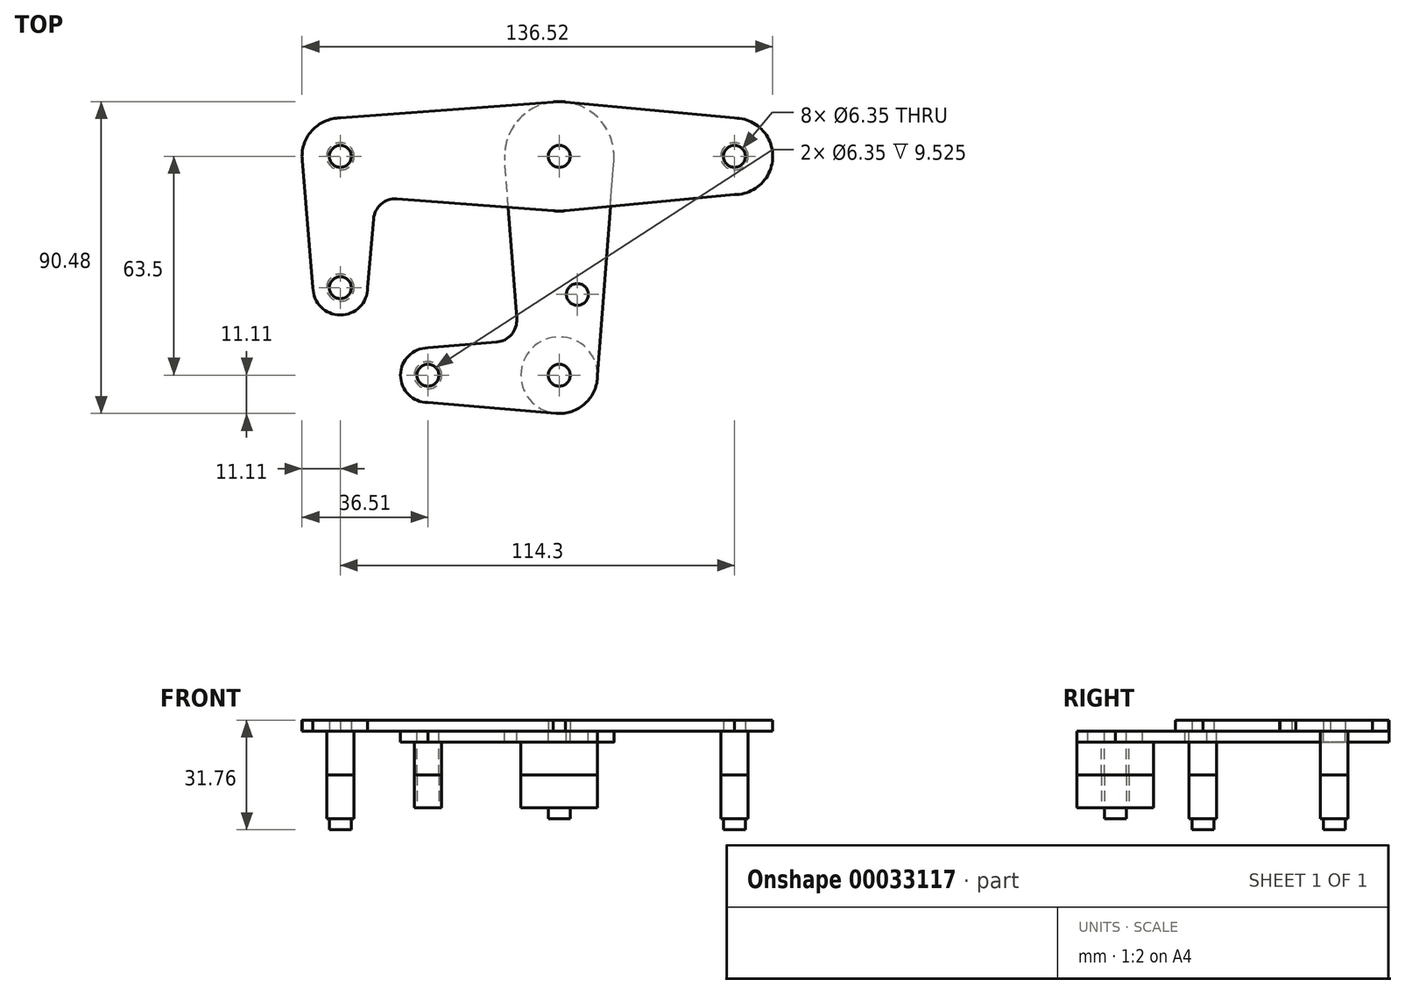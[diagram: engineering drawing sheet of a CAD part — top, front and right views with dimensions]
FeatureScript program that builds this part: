
annotation { "Feature Type Name" : "Feature", "Feature Type Description" : "" }
export const myFeature = defineFeature(function(context is Context, id is Id, definition is map)
    precondition{}
    {
        {
            var Q0;
            Q0=qCreatedBy(makeId("Top.planeOp"),FACE);
            var sketch = newSketch(context, id + "F0", { "sketchPlane" : qUnion([Q0])});
            skCircle(sketch, "E0", {"center": v(0, 0) * mm, "radius": 3.18 * mm});
            skCircle(sketch, "E1", {"center": v(-63.5, 0) * mm, "radius": 3.18 * mm});
            skCircle(sketch, "E2", {"center": v(50.8, 0) * mm, "radius": 3.18 * mm});
            skCircle(sketch, "E3", {"center": v(-63.5, -38.1) * mm, "radius": 3.18 * mm});
            skCircle(sketch, "E4", {"center": v(0, 0) * mm, "radius": 15.88 * mm});
            skCircle(sketch, "E5", {"center": v(-63.5, 0) * mm, "radius": 11.11 * mm});
            skCircle(sketch, "E6", {"center": v(50.8, 0) * mm, "radius": 11.11 * mm});
            skCircle(sketch, "E7", {"center": v(-63.5, -38.1) * mm, "radius": 7.94 * mm});
            skCircle(sketch, "E8", {"center": v(0, -63.5) * mm, "radius": 3.18 * mm});
            skCircle(sketch, "E9", {"center": v(0, -63.5) * mm, "radius": 11.11 * mm});
            skCircle(sketch, "E10", {"center": v(-38.1, -63.5) * mm, "radius": 3.18 * mm});
            skCircle(sketch, "E11", {"center": v(-38.1, -63.5) * mm, "radius": 7.94 * mm});
            skLineSegment(sketch, "E12", {"start": v(1.8, 15.77) * mm, "end": v(50.77, 11.11) * mm});
            skLineSegment(sketch, "E13.MirrorCS", {"start": v(1.8, -15.77) * mm, "end": v(50.77, -11.11) * mm});
            skLineSegment(sketch, "E14.MirrorCS", {"start": v(-1.8, 15.77) * mm, "end": v(-63.5, 11.11) * mm});
            skLineSegment(sketch, "E15.MirrorCS", {"start": v(-1.8, -15.77) * mm, "end": v(-47.07, -12.35) * mm});
            skLineSegment(sketch, "E16", {"start": v(-71.44, -38.1) * mm, "end": v(-74.55, -1.16) * mm});
            skLineSegment(sketch, "E17.MirrorCS", {"start": v(-55.56, -38.1) * mm, "end": v(-53.88, -18.15) * mm});
            skArc(sketch, "E18.filletArc", {"start": v(-47.07, -12.35) * mm, "mid": v(-51.67, -13.85) * mm, "end": v(-53.88, -18.15) * mm});
            skLineSegment(sketch, "E19", {"start": v(-12.36, -47.07) * mm, "end": v(-15.83, -1.2) * mm});
            skLineSegment(sketch, "E20.MirrorCS", {"start": v(11.11, -63.5) * mm, "end": v(15.83, -1.2) * mm});
            skLineSegment(sketch, "E21", {"start": v(-38.1, -55.56) * mm, "end": v(-18.15, -53.88) * mm});
            skLineSegment(sketch, "E22.MirrorCS", {"start": v(-38.1, -71.44) * mm, "end": v(-0.93, -74.57) * mm});
            skArc(sketch, "E23.filletArc", {"start": v(-18.15, -53.88) * mm, "mid": v(-13.85, -51.67) * mm, "end": v(-12.36, -47.07) * mm});
            skCircle(sketch, "E24", {"center": v(5.25, -40.08) * mm, "radius": 3.18 * mm});
            skSolve(sketch);
        }
        {
            var Q0;
            {var subQ3=sQuery(id+"F0.wireOp",EDGE,"E14.MirrorCS");Q0=makeQuery(id+"F0.imprint","IMPRINT",FACE,{"disambiguationData":[TD([[makeQuery(id+"F0.imprint","IMPRINT",EDGE,{"derivedFrom":subQ3}),1.0]])]});}
            var Q1;
            Q1=makeQuery(id+"F0.imprint","IMPRINT",FACE,{"disambiguationData":[TD([[makeQuery(id+"F0.imprint","IMPRINT",EDGE,{"derivedFrom":sQuery(id+"F0.wireOp",EDGE,"E1")}),-1.0]])]});
            var Q2;
            Q2=makeQuery(id+"F0.imprint","IMPRINT",FACE,{"disambiguationData":[TD([[makeQuery(id+"F0.imprint","IMPRINT",EDGE,{"derivedFrom":sQuery(id+"F0.wireOp",EDGE,"E3")}),-1.0]])]});
            var Q3;
            Q3=makeQuery(id+"F0.imprint","IMPRINT",FACE,{"disambiguationData":[TD([[makeQuery(id+"F0.imprint","IMPRINT",EDGE,{"derivedFrom":sQuery(id+"F0.wireOp",EDGE,"E0")}),-1.0]])]});
            var Q4;
            {var subQ0=sQuery(id+"F0.wireOp",EDGE,"E15.MirrorCS");var subQ1=sQuery(id+"F0.wireOp",EDGE,"E4");var subQ2=makeQuery(id+"F0.imprint","INTERSECT",VERTEX,{"derivedFrom":[subQ1,subQ0]});Q4=makeQuery(id+"F0.imprint","IMPRINT",FACE,{"disambiguationData":[TD([[makeQuery(id+"F0.imprint","IMPRINT",EDGE,{"disambiguationData":[TD([[subQ2,1.0]])],"derivedFrom":subQ1}),-1.0]])]});}
            var Q5;
            {var subQ0=sQuery(id+"F0.wireOp",EDGE,"E13.MirrorCS");var subQ1=sQuery(id+"F0.wireOp",EDGE,"E4");var subQ2=makeQuery(id+"F0.imprint","INTERSECT",VERTEX,{"derivedFrom":[subQ1,subQ0]});Q5=makeQuery(id+"F0.imprint","IMPRINT",FACE,{"disambiguationData":[TD([[makeQuery(id+"F0.imprint","IMPRINT",EDGE,{"disambiguationData":[TD([[subQ2,-1.0]])],"derivedFrom":subQ1}),-1.0]])]});}
            var Q6;
            {var subQ0=sQuery(id+"F0.wireOp",EDGE,"E12");Q6=makeQuery(id+"F0.imprint","IMPRINT",FACE,{"disambiguationData":[TD([[makeQuery(id+"F0.imprint","IMPRINT",EDGE,{"derivedFrom":subQ0}),-1.0]])]});}
            var Q7;
            Q7=makeQuery(id+"F0.imprint","IMPRINT",FACE,{"disambiguationData":[TD([[makeQuery(id+"F0.imprint","IMPRINT",EDGE,{"derivedFrom":sQuery(id+"F0.wireOp",EDGE,"E2")}),-1.0]])]});
            extrude(context, id + "F1", {"entities" : qUnion([Q0, Q1, Q2, Q3, Q4, Q5, Q6, Q7]), "depth" : 3.17 * mm});
        }
        {
            var Q0;
            {var subQ0=sQuery(id+"F0.wireOp",EDGE,"E13.MirrorCS");var subQ1=sQuery(id+"F0.wireOp",EDGE,"E4");var subQ2=makeQuery(id+"F0.imprint","INTERSECT",VERTEX,{"derivedFrom":[subQ1,subQ0]});Q0=makeQuery(id+"F0.imprint","IMPRINT",FACE,{"disambiguationData":[TD([[makeQuery(id+"F0.imprint","IMPRINT",EDGE,{"disambiguationData":[TD([[subQ2,-1.0]])],"derivedFrom":subQ1}),-1.0]])]});}
            var Q1;
            {var subQ0=sQuery(id+"F0.wireOp",EDGE,"E15.MirrorCS");var subQ1=sQuery(id+"F0.wireOp",EDGE,"E4");var subQ2=makeQuery(id+"F0.imprint","INTERSECT",VERTEX,{"derivedFrom":[subQ1,subQ0]});Q1=makeQuery(id+"F0.imprint","IMPRINT",FACE,{"disambiguationData":[TD([[makeQuery(id+"F0.imprint","IMPRINT",EDGE,{"disambiguationData":[TD([[subQ2,1.0]])],"derivedFrom":subQ1}),-1.0]])]});}
            var Q2;
            Q2=makeQuery(id+"F0.imprint","IMPRINT",FACE,{"disambiguationData":[TD([[makeQuery(id+"F0.imprint","IMPRINT",EDGE,{"derivedFrom":sQuery(id+"F0.wireOp",EDGE,"E0")}),-1.0]])]});
            var Q3;
            {var subQ1=sQuery(id+"F0.wireOp",EDGE,"E21");Q3=makeQuery(id+"F0.imprint","IMPRINT",FACE,{"disambiguationData":[TD([[makeQuery(id+"F0.imprint","IMPRINT",EDGE,{"derivedFrom":subQ1}),-1.0]])]});}
            var Q4;
            Q4=makeQuery(id+"F0.imprint","IMPRINT",FACE,{"disambiguationData":[TD([[makeQuery(id+"F0.imprint","IMPRINT",EDGE,{"derivedFrom":sQuery(id+"F0.wireOp",EDGE,"E8")}),-1.0]])]});
            var Q5;
            Q5=makeQuery(id+"F0.imprint","IMPRINT",FACE,{"disambiguationData":[TD([[makeQuery(id+"F0.imprint","IMPRINT",EDGE,{"derivedFrom":sQuery(id+"F0.wireOp",EDGE,"E10")}),-1.0]])]});
            extrude(context, id + "F2", {"entities" : qUnion([Q0, Q1, Q2, Q3, Q4, Q5]), "oppositeDirection" : true, "depth" : 3.17 * mm});
        }
        {
            var Q0;
            Q0=makeQuery(id+"F1.opExtrude","CAP_FACE",FACE,{"disambiguationData":[OSD([sQuery(id+"F0.wireOp",EDGE,"E0"),sQuery(id+"F0.wireOp",EDGE,"E1"),sQuery(id+"F0.wireOp",EDGE,"E2"),sQuery(id+"F0.wireOp",EDGE,"E3"),sQuery(id+"F0.wireOp",EDGE,"E4"),sQuery(id+"F0.wireOp",EDGE,"E5"),sQuery(id+"F0.wireOp",EDGE,"E6"),sQuery(id+"F0.wireOp",EDGE,"E7"),sQuery(id+"F0.wireOp",EDGE,"E12"),sQuery(id+"F0.wireOp",EDGE,"E13.MirrorCS"),sQuery(id+"F0.wireOp",EDGE,"E14.MirrorCS"),sQuery(id+"F0.wireOp",EDGE,"E15.MirrorCS"),sQuery(id+"F0.wireOp",EDGE,"E16"),sQuery(id+"F0.wireOp",EDGE,"E17.MirrorCS"),sQuery(id+"F0.wireOp",EDGE,"E18.filletArc")])],"isStart":false});
            var sketch = newSketch(context, id + "F3", { "sketchPlane" : qUnion([Q0])});
            skCircle(sketch, "E25", {"center": v(-63.5, 0) * mm, "radius": 3.97 * mm});
            skCircle(sketch, "E26", {"center": v(0, 0) * mm, "radius": 3.97 * mm});
            skCircle(sketch, "E27", {"center": v(50.8, 0) * mm, "radius": 3.97 * mm});
            skCircle(sketch, "E28", {"center": v(-63.5, -38.1) * mm, "radius": 3.97 * mm});
            skCircle(sketch, "E29", {"center": v(50.8, 0) * mm, "radius": 11.11 * mm});
            skCircle(sketch, "E30", {"center": v(-63.5, 0) * mm, "radius": 11.11 * mm});
            skCircle(sketch, "E31", {"center": v(-63.5, -38.1) * mm, "radius": 7.94 * mm});
            skSolve(sketch);
        }
        {
            var Q0;
            Q0=makeQuery(id+"F2.opExtrude","CAP_FACE",FACE,{"disambiguationData":[OSD([sQuery(id+"F0.wireOp",EDGE,"E0"),sQuery(id+"F0.wireOp",EDGE,"E4"),sQuery(id+"F0.wireOp",EDGE,"E8"),sQuery(id+"F0.wireOp",EDGE,"E9"),sQuery(id+"F0.wireOp",EDGE,"E10"),sQuery(id+"F0.wireOp",EDGE,"E11"),sQuery(id+"F0.wireOp",EDGE,"E19"),sQuery(id+"F0.wireOp",EDGE,"E20.MirrorCS"),sQuery(id+"F0.wireOp",EDGE,"E21"),sQuery(id+"F0.wireOp",EDGE,"E22.MirrorCS"),sQuery(id+"F0.wireOp",EDGE,"E23.filletArc"),sQuery(id+"F0.wireOp",EDGE,"E24")])],"isStart":true});
            var sketch = newSketch(context, id + "F4", { "sketchPlane" : qUnion([Q0])});
            skCircle(sketch, "E32", {"center": v(0, -63.5) * mm, "radius": 3.97 * mm});
            skCircle(sketch, "E33", {"center": v(-38.1, -63.5) * mm, "radius": 3.97 * mm});
            skCircle(sketch, "E34", {"center": v(0, -63.5) * mm, "radius": 11.11 * mm});
            skCircle(sketch, "E35", {"center": v(-38.1, -63.5) * mm, "radius": 7.94 * mm});
            skSolve(sketch);
        }
        {
            var Q0;
            Q0=qCreatedBy(makeId("Top.planeOp"),FACE);
            cPlane(context, id + "F5", {"entities" : qUnion([Q0]), "cplaneType" : CPlaneType.OFFSET, "offset" : 12.7 * mm, "oppositeDirection" : true, "width" : 152.4 * mm, "height" : 152.4 * mm});
        }
        {
            var Q0;
            Q0=makeQuery(id+"F3.imprint","IMPRINT",FACE,{"disambiguationData":[TD([[makeQuery(id+"F3.imprint","IMPRINT",EDGE,{"derivedFrom":sQuery(id+"F3.wireOp",EDGE,"E25")}),1.0]])]});
            var Q1;
            Q1=makeQuery(id+"F3.imprint","IMPRINT",FACE,{"disambiguationData":[TD([[makeQuery(id+"F3.imprint","IMPRINT",EDGE,{"derivedFrom":makeQuery(id+"F1.opExtrude","CAP_EDGE",EDGE,{"disambiguationData":[OSD([sQuery(id+"F0.wireOp",EDGE,"E1")])],"isStart":false})}),1.0]])]});
            var Q2;
            Q2=makeQuery(id+"F3.imprint","IMPRINT",FACE,{"disambiguationData":[TD([[makeQuery(id+"F3.imprint","IMPRINT",EDGE,{"derivedFrom":makeQuery(id+"F1.opExtrude","CAP_EDGE",EDGE,{"disambiguationData":[OSD([sQuery(id+"F0.wireOp",EDGE,"E3")])],"isStart":false})}),1.0]])]});
            var Q3;
            Q3=makeQuery(id+"F3.imprint","IMPRINT",FACE,{"disambiguationData":[TD([[makeQuery(id+"F3.imprint","IMPRINT",EDGE,{"derivedFrom":sQuery(id+"F3.wireOp",EDGE,"E28")}),1.0]])]});
            var Q4;
            Q4=makeQuery(id+"F4.imprint","IMPRINT",FACE,{"disambiguationData":[TD([[makeQuery(id+"F4.imprint","IMPRINT",EDGE,{"derivedFrom":sQuery(id+"F4.wireOp",EDGE,"E33")}),1.0]])]});
            var Q5;
            Q5=makeQuery(id+"F0.imprint","IMPRINT",FACE,{"disambiguationData":[TD([[makeQuery(id+"F0.imprint","IMPRINT",EDGE,{"derivedFrom":sQuery(id+"F0.wireOp",EDGE,"E8")}),-1.0]])]});
            var Q6;
            Q6=makeQuery(id+"F0.imprint","IMPRINT",FACE,{"disambiguationData":[TD([[makeQuery(id+"F0.imprint","IMPRINT",EDGE,{"derivedFrom":sQuery(id+"F0.wireOp",EDGE,"E8")}),1.0]])]});
            var Q7;
            Q7=makeQuery(id+"F3.imprint","IMPRINT",FACE,{"disambiguationData":[TD([[makeQuery(id+"F3.imprint","IMPRINT",EDGE,{"derivedFrom":makeQuery(id+"F1.opExtrude","CAP_EDGE",EDGE,{"disambiguationData":[OSD([sQuery(id+"F0.wireOp",EDGE,"E2")])],"isStart":false})}),1.0]])]});
            var Q8;
            Q8=makeQuery(id+"F3.imprint","IMPRINT",FACE,{"disambiguationData":[TD([[makeQuery(id+"F3.imprint","IMPRINT",EDGE,{"derivedFrom":sQuery(id+"F3.wireOp",EDGE,"E27")}),1.0]])]});
            var Q9;
            Q9=makeQuery(id+"F0.imprint","IMPRINT",FACE,{"disambiguationData":[TD([[makeQuery(id+"F0.imprint","IMPRINT",EDGE,{"derivedFrom":sQuery(id+"F0.wireOp",EDGE,"E10")}),1.0]])]});
            var Q10;
            Q10=qCreatedBy(id+"F5.planeOp",FACE);
            extrude(context, id + "F6", {"entities" : qUnion([Q0, Q1, Q2, Q3, Q4, Q5, Q6, Q7, Q8, Q9]), "endBound" : BoundingType.UP_TO_SURFACE, "oppositeDirection" : true, "endBoundEntityFace" : qUnion([Q10]), "depth" : 25.4 * mm});
        }
        {
            var Q0;
            Q0=makeQuery(id+"F1.opExtrude","SWEPT_BODY",BODY,{"disambiguationData":[OSD([sQuery(id+"F0.wireOp",EDGE,"E0"),sQuery(id+"F0.wireOp",EDGE,"E1"),sQuery(id+"F0.wireOp",EDGE,"E2"),sQuery(id+"F0.wireOp",EDGE,"E3"),sQuery(id+"F0.wireOp",EDGE,"E4"),sQuery(id+"F0.wireOp",EDGE,"E5"),sQuery(id+"F0.wireOp",EDGE,"E6"),sQuery(id+"F0.wireOp",EDGE,"E7"),sQuery(id+"F0.wireOp",EDGE,"E12"),sQuery(id+"F0.wireOp",EDGE,"E13.MirrorCS"),sQuery(id+"F0.wireOp",EDGE,"E14.MirrorCS"),sQuery(id+"F0.wireOp",EDGE,"E15.MirrorCS"),sQuery(id+"F0.wireOp",EDGE,"E16"),sQuery(id+"F0.wireOp",EDGE,"E17.MirrorCS"),sQuery(id+"F0.wireOp",EDGE,"E18.filletArc")])]});
            var Q1;
            Q1=makeQuery(id+"F2.opExtrude","SWEPT_BODY",BODY,{"disambiguationData":[OSD([sQuery(id+"F0.wireOp",EDGE,"E0"),sQuery(id+"F0.wireOp",EDGE,"E4"),sQuery(id+"F0.wireOp",EDGE,"E8"),sQuery(id+"F0.wireOp",EDGE,"E9"),sQuery(id+"F0.wireOp",EDGE,"E10"),sQuery(id+"F0.wireOp",EDGE,"E11"),sQuery(id+"F0.wireOp",EDGE,"E19"),sQuery(id+"F0.wireOp",EDGE,"E20.MirrorCS"),sQuery(id+"F0.wireOp",EDGE,"E21"),sQuery(id+"F0.wireOp",EDGE,"E22.MirrorCS"),sQuery(id+"F0.wireOp",EDGE,"E23.filletArc"),sQuery(id+"F0.wireOp",EDGE,"E24")])]});
            var Q2;
            Q2=makeQuery(id+"F6.opExtrude","SWEPT_BODY",BODY,{"disambiguationData":[OSD([sQuery(id+"F3.wireOp",EDGE,"E25")])]});
            var Q3;
            Q3=makeQuery(id+"F6.opExtrude","SWEPT_BODY",BODY,{"disambiguationData":[OSD([sQuery(id+"F3.wireOp",EDGE,"E28")])]});
            var Q4;
            Q4=makeQuery(id+"F6.opExtrude","SWEPT_BODY",BODY,{"disambiguationData":[OSD([sQuery(id+"F0.wireOp",EDGE,"E10"),sQuery(id+"F4.wireOp",EDGE,"E33")])]});
            var Q5;
            Q5=makeQuery(id+"F6.opExtrude","SWEPT_BODY",BODY,{"disambiguationData":[OSD([sQuery(id+"F0.wireOp",EDGE,"E9")])]});
            var Q6;
            Q6=makeQuery(id+"F6.opExtrude","SWEPT_BODY",BODY,{"disambiguationData":[OSD([sQuery(id+"F3.wireOp",EDGE,"E29")])]});
            var Q7;
            Q7=makeQuery(id+"F6.opExtrude","SWEPT_BODY",BODY,{"disambiguationData":[OSD([sQuery(id+"F3.wireOp",EDGE,"E27")])]});
            booleanBodies(context, id + "F7", {"operationType" : BooleanOperationType.SUBTRACTION, "tools" : qUnion([Q0, Q1]), "targets" : qUnion([Q2, Q3, Q4, Q5, Q6, Q7]), "keepTools" : true});
        }
        {
            var Q0;
            Q0=makeQuery(id+"F6.opExtrude","SWEPT_BODY",BODY,{"disambiguationData":[OSD([sQuery(id+"F3.wireOp",EDGE,"E28")])]});
            var Q1;
            Q1=makeQuery(id+"F6.opExtrude","SWEPT_BODY",BODY,{"disambiguationData":[OSD([sQuery(id+"F3.wireOp",EDGE,"E25")])]});
            var Q2;
            Q2=makeQuery(id+"F6.opExtrude","SWEPT_BODY",BODY,{"disambiguationData":[OSD([sQuery(id+"F0.wireOp",EDGE,"E10"),sQuery(id+"F4.wireOp",EDGE,"E33")])]});
            var Q3;
            Q3=makeQuery(id+"F6.opExtrude","SWEPT_BODY",BODY,{"disambiguationData":[OSD([sQuery(id+"F0.wireOp",EDGE,"E9")])]});
            var Q4;
            Q4=makeQuery(id+"F6.opExtrude","SWEPT_BODY",BODY,{"disambiguationData":[OSD([sQuery(id+"F3.wireOp",EDGE,"E27")])]});
            var Q5;
            Q5=qCreatedBy(id+"F5.planeOp",FACE);
            mirror(context, id + "F8", {"entities" : qUnion([Q0, Q1, Q2, Q3, Q4]), "mirrorPlane" : qUnion([Q5])});
        }
    });
